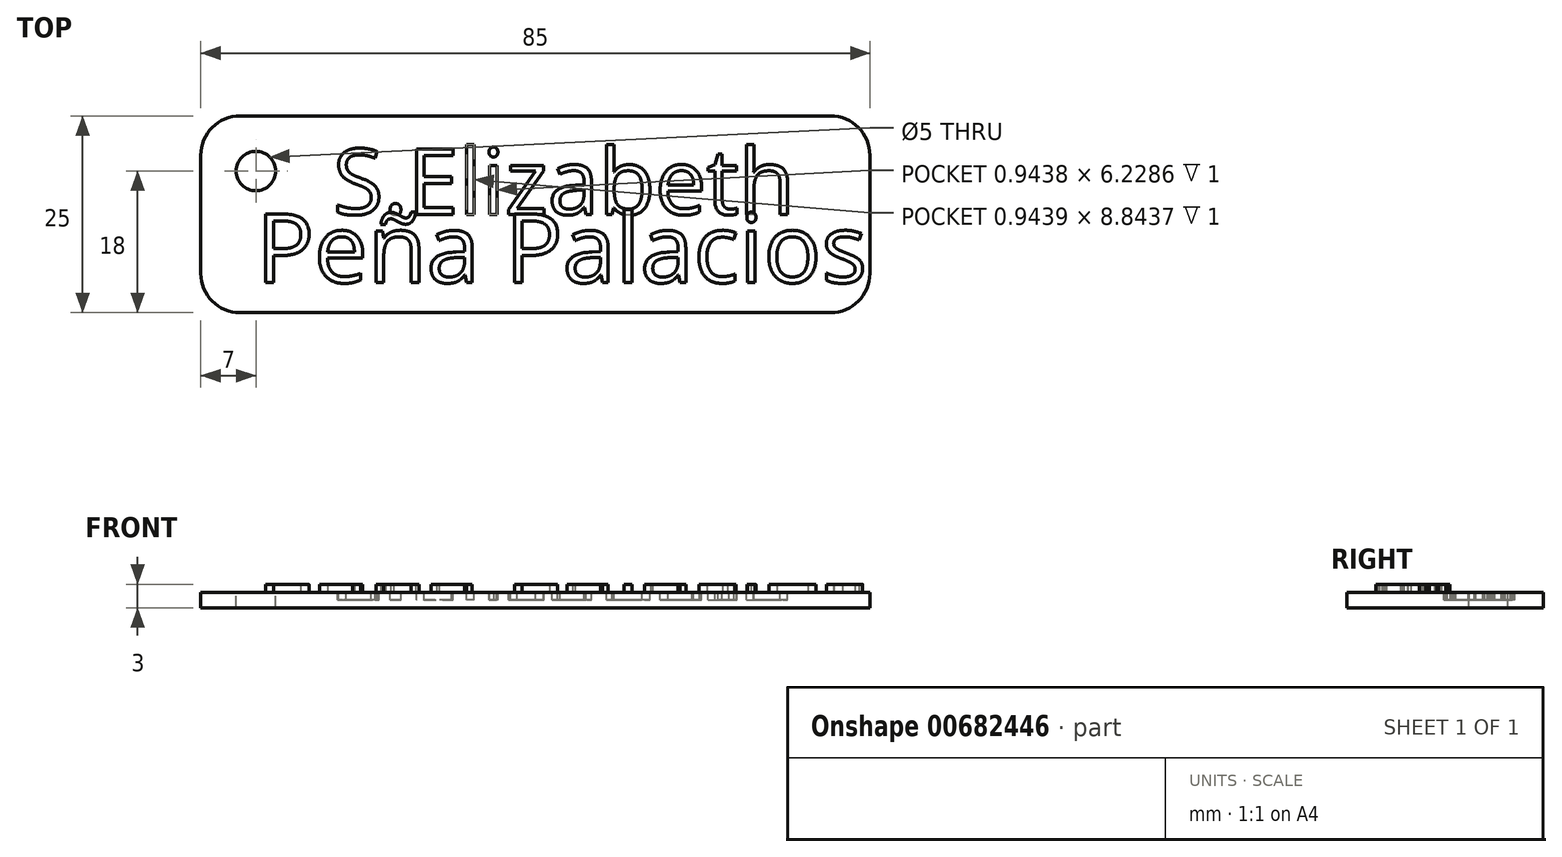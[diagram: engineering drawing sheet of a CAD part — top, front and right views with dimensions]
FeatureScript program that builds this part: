
annotation { "Feature Type Name" : "Feature", "Feature Type Description" : "" }
export const myFeature = defineFeature(function(context is Context, id is Id, definition is map)
    precondition{}
    {
        {
            var Q0;
            Q0=qCreatedBy(makeId("Top.planeOp"),FACE);
            var sketch = newSketch(context, id + "F0", { "sketchPlane" : qUnion([Q0])});
            skLineSegment(sketch, "E0.bottom", {"start": v(-37.5, 12.5) * mm, "end": v(37.5, 12.5) * mm});
            skLineSegment(sketch, "E0.top", {"start": v(-37.5, -12.5) * mm, "end": v(37.5, -12.5) * mm});
            skLineSegment(sketch, "E0.left", {"start": v(-42.5, 7.5) * mm, "end": v(-42.5, -7.5) * mm});
            skLineSegment(sketch, "E0.right", {"start": v(42.5, 7.5) * mm, "end": v(42.5, -7.5) * mm});
            skPoint(sketch, "E0.middle", {"position": v(0, 0) * mm});
            skPoint(sketch, "E1.visualSharp", {"position": v(-42.5, 12.5) * mm});
            skArc(sketch, "E1.filletArc", {"start": v(-37.5, 12.5) * mm, "mid": v(-41.04, 11.04) * mm, "end": v(-42.5, 7.5) * mm});
            skPoint(sketch, "E2.visualSharp", {"position": v(-42.5, -12.5) * mm});
            skArc(sketch, "E2.filletArc", {"start": v(-42.5, -7.5) * mm, "mid": v(-41.04, -11.04) * mm, "end": v(-37.5, -12.5) * mm});
            skPoint(sketch, "E3.visualSharp", {"position": v(42.5, -12.5) * mm});
            skArc(sketch, "E3.filletArc", {"start": v(37.5, -12.5) * mm, "mid": v(41.04, -11.04) * mm, "end": v(42.5, -7.5) * mm});
            skPoint(sketch, "E4.visualSharp", {"position": v(42.5, 12.5) * mm});
            skArc(sketch, "E4.filletArc", {"start": v(42.5, 7.5) * mm, "mid": v(41.04, 11.04) * mm, "end": v(37.5, 12.5) * mm});
            skSolve(sketch);
        }
        {
            var Q0;
            Q0=makeQuery(id+"F0.imprint","IMPRINT",FACE,{"disambiguationData":[TD([[makeQuery(id+"F0.imprint","IMPRINT",EDGE,{"derivedFrom":sQuery(id+"F0.wireOp",EDGE,"E0.bottom")}),-1.0]])]});
            extrude(context, id + "F1", {"entities" : qUnion([Q0]), "depth" : 2 * mm, "offsetDistance" : 25 * mm});
        }
        {
            var Q0;
            Q0=makeQuery(id+"F1.opExtrude","CAP_FACE",FACE,{"disambiguationData":[OSD([sQuery(id+"F0.wireOp",EDGE,"E0.bottom"),sQuery(id+"F0.wireOp",EDGE,"E0.top"),sQuery(id+"F0.wireOp",EDGE,"E0.left"),sQuery(id+"F0.wireOp",EDGE,"E0.right"),sQuery(id+"F0.wireOp",EDGE,"E1.filletArc"),sQuery(id+"F0.wireOp",EDGE,"E2.filletArc"),sQuery(id+"F0.wireOp",EDGE,"E3.filletArc"),sQuery(id+"F0.wireOp",EDGE,"E4.filletArc")])],"isStart":false});
            var sketch = newSketch(context, id + "F2", { "sketchPlane" : qUnion([Q0])});
            skPoint(sketch, "E5", {"position": v(-35.5, 5.5) * mm});
            skSolve(sketch);
        }
        {
            var Q0;
            Q0=sQuery(id+"F2.wireOp",VERTEX,"E5");
            var Q1;
            Q1=makeQuery(id+"F1.opExtrude","SWEPT_BODY",BODY,{"disambiguationData":[OSD([sQuery(id+"F0.wireOp",EDGE,"E0.bottom"),sQuery(id+"F0.wireOp",EDGE,"E0.top"),sQuery(id+"F0.wireOp",EDGE,"E0.left"),sQuery(id+"F0.wireOp",EDGE,"E0.right"),sQuery(id+"F0.wireOp",EDGE,"E1.filletArc"),sQuery(id+"F0.wireOp",EDGE,"E2.filletArc"),sQuery(id+"F0.wireOp",EDGE,"E3.filletArc"),sQuery(id+"F0.wireOp",EDGE,"E4.filletArc")])]});
            hole(context, id + "F3", {"style" : HoleStyle.SIMPLE, "endStyle" : HoleEndStyle.THROUGH, "holeDiameter" : 5 * mm, "majorDiameter" : 5 * mm, "isTappedThrough" : true, "tappedDepth" : 12 * mm, "tapClearance" : 3, "locations" : qUnion([Q0]), "scope" : qUnion([Q1])});
        }
        {
            var Q0;
            Q0=makeQuery(id+"F1.opExtrude","CAP_FACE",FACE,{"disambiguationData":[OSD([sQuery(id+"F0.wireOp",EDGE,"E0.bottom"),sQuery(id+"F0.wireOp",EDGE,"E0.top"),sQuery(id+"F0.wireOp",EDGE,"E0.left"),sQuery(id+"F0.wireOp",EDGE,"E0.right"),sQuery(id+"F0.wireOp",EDGE,"E1.filletArc"),sQuery(id+"F0.wireOp",EDGE,"E2.filletArc"),sQuery(id+"F0.wireOp",EDGE,"E3.filletArc"),sQuery(id+"F0.wireOp",EDGE,"E4.filletArc")])],"isStart":false});
            var sketch = newSketch(context, id + "F4", { "sketchPlane" : qUnion([Q0])});
            skText(sketch, "E6", { "text": "S.Elizabeth", "fontName": "OpenSans-Regular.ttf"});
            const initialGuessF4  = {"E6": [-0.0257, 0, 1, 0, 0.00838]};
            skSetInitialGuess(sketch, initialGuessF4);
            skSolve(sketch);
        }
        {
            var Q0;
            Q0 = qSketchRegion(id + "F4", true);
            extrude(context, id + "F5", {"entities" : qUnion([Q0]), "operationType" : NewBodyOperationType.REMOVE, "oppositeDirection" : true, "depth" : 1 * mm, "offsetDistance" : 25 * mm});
        }
        {
            var Q0;
            {var subQ0=sQuery(id+"F0.wireOp",EDGE,"E0.bottom");var subQ1=sQuery(id+"F0.wireOp",EDGE,"E1.filletArc");var subQ2=sQuery(id+"F0.wireOp",EDGE,"E2.filletArc");var subQ3=sQuery(id+"F0.wireOp",EDGE,"E4.filletArc");var subQ4=sQuery(id+"F0.wireOp",EDGE,"E0.left");var subQ5=sQuery(id+"F0.wireOp",EDGE,"E3.filletArc");var subQ6=sQuery(id+"F0.wireOp",EDGE,"E0.top");var subQ7=sQuery(id+"F0.wireOp",EDGE,"E0.right");Q0=makeQuery(id+"F5.boolean.opBoolean","SPLIT",FACE,{"disambiguationData":[TD([makeQuery(id+"F1.opExtrude","SWEPT_FACE",FACE,{"disambiguationData":[OSD([subQ0])]})])],"derivedFrom":makeQuery(id+"F1.opExtrude","CAP_FACE",FACE,{"disambiguationData":[OSD([subQ0,subQ6,subQ4,subQ7,subQ1,subQ2,subQ5,subQ3])],"isStart":false})});}
            var sketch = newSketch(context, id + "F6", { "sketchPlane" : qUnion([Q0])});
            skText(sketch, "E7", { "text": "Peña Palacios\n", "fontName": "OpenSans-Regular.ttf"});
            const initialGuessF6  = {"E7": [-0.03545, -0.00866, 1, 0, 0.00877]};
            skSetInitialGuess(sketch, initialGuessF6);
            skSolve(sketch);
        }
        {
            var Q0;
            Q0 = qSketchRegion(id + "F6", true);
            extrude(context, id + "F7", {"entities" : qUnion([Q0]), "operationType" : NewBodyOperationType.ADD, "depth" : 1 * mm, "offsetDistance" : 25 * mm});
        }
    });
